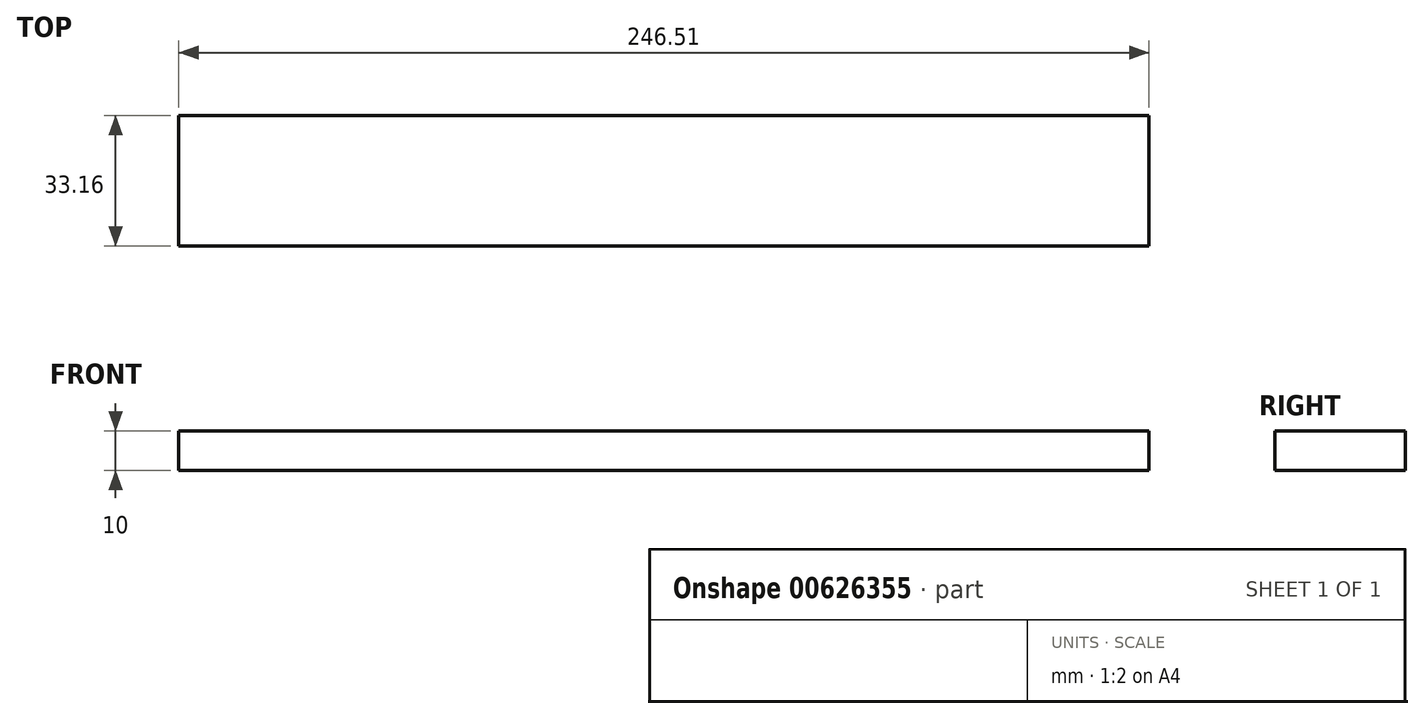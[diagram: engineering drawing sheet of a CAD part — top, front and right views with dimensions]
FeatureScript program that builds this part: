
annotation { "Feature Type Name" : "Feature", "Feature Type Description" : "" }
export const myFeature = defineFeature(function(context is Context, id is Id, definition is map)
    precondition{}
    {
        {
            var Q0;
            Q0=qCreatedBy(makeId("Top.planeOp"),FACE);
            var sketch = newSketch(context, id + "F0", { "sketchPlane" : qUnion([Q0])});
            skLineSegment(sketch, "E0.bottom", {"start": v(-117.94, 38.22) * mm, "end": v(128.57, 38.22) * mm});
            skLineSegment(sketch, "E0.top", {"start": v(-117.94, 5.06) * mm, "end": v(128.57, 5.06) * mm});
            skLineSegment(sketch, "E0.left", {"start": v(-117.94, 38.22) * mm, "end": v(-117.94, 5.06) * mm});
            skLineSegment(sketch, "E0.right", {"start": v(128.57, 38.22) * mm, "end": v(128.57, 5.06) * mm});
            skSolve(sketch);
        }
        {
            var Q0;
            Q0=qSketchRegion(id+"F0",true);
            extrude(context, id + "F1", {"entities" : qUnion([Q0]), "depth" : 10 * mm});
        }
    });
